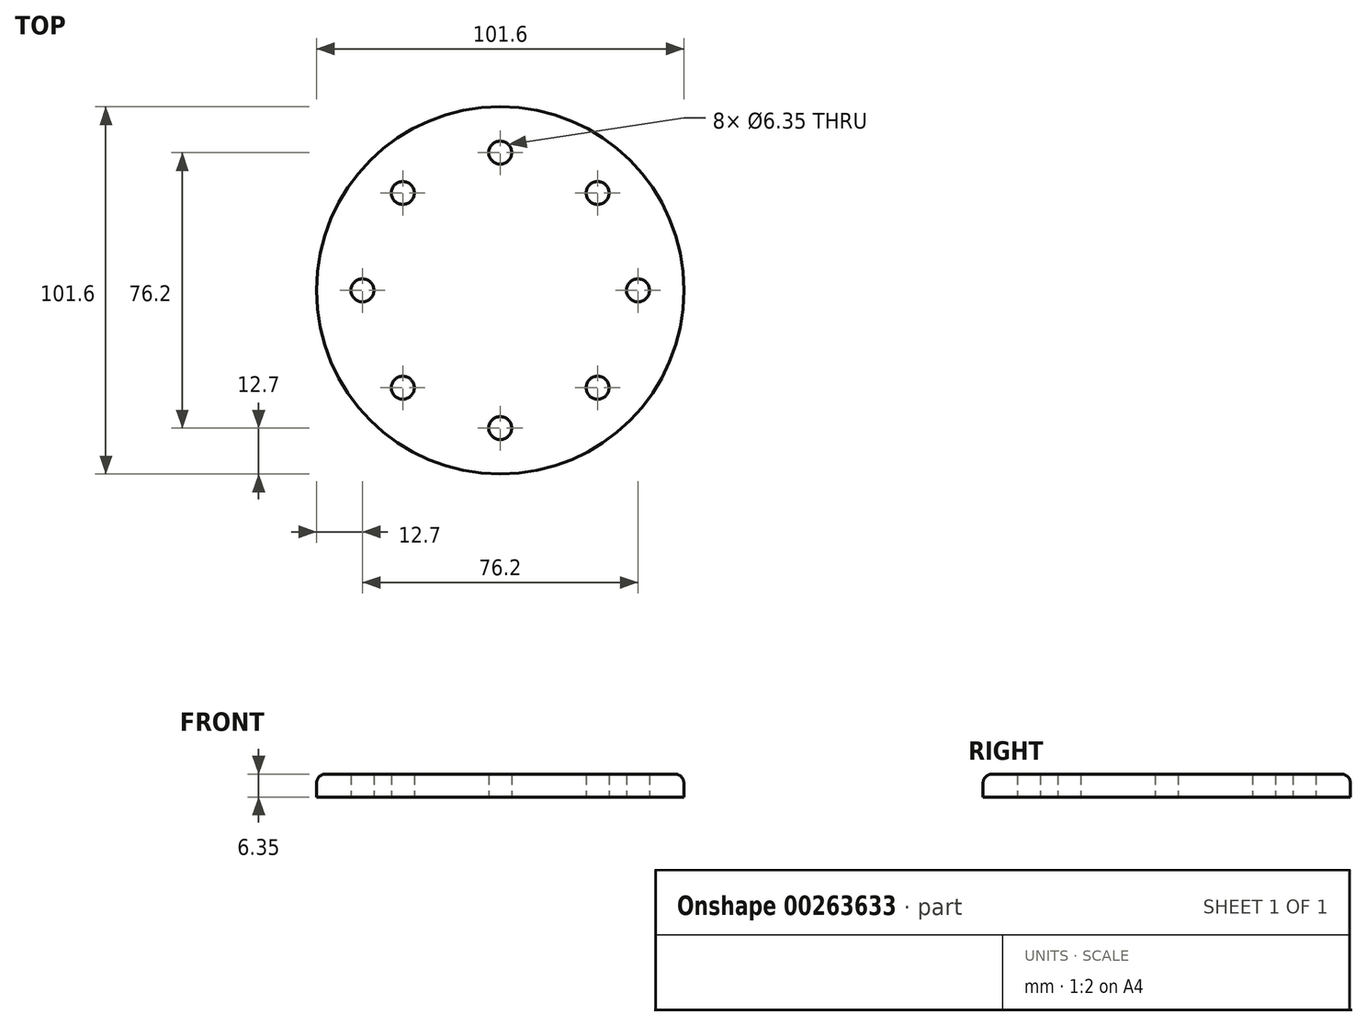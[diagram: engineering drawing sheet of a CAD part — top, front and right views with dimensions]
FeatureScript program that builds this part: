
annotation { "Feature Type Name" : "Feature", "Feature Type Description" : "" }
export const myFeature = defineFeature(function(context is Context, id is Id, definition is map)
    precondition{}
    {
        {
            var Q0;
            Q0=qCreatedBy(makeId("Top.planeOp"),FACE);
            var sketch = newSketch(context, id + "F0", { "sketchPlane" : qUnion([Q0])});
            skCircle(sketch, "E0", {"center": v(0, 0) * mm, "radius": 50.8 * mm});
            skCircle(sketch, "E1", {"center": v(-38.1, 0) * mm, "radius": 3.18 * mm});
            skCircle(sketch, "E2", {"center": v(-26.94, -26.94) * mm, "radius": 3.18 * mm});
            skCircle(sketch, "E3", {"center": v(0, -38.1) * mm, "radius": 3.18 * mm});
            skCircle(sketch, "E4", {"center": v(26.94, -26.94) * mm, "radius": 3.18 * mm});
            skCircle(sketch, "E5", {"center": v(38.1, 0) * mm, "radius": 3.18 * mm});
            skCircle(sketch, "E6", {"center": v(26.94, 26.94) * mm, "radius": 3.18 * mm});
            skCircle(sketch, "E7", {"center": v(0, 38.1) * mm, "radius": 3.18 * mm});
            skCircle(sketch, "E8", {"center": v(-26.94, 26.94) * mm, "radius": 3.18 * mm});
            skSolve(sketch);
        }
        {
            var Q0;
            Q0=makeQuery(id+"F0.imprint","IMPRINT",FACE,{"disambiguationData":[TD([[makeQuery(id+"F0.imprint","IMPRINT",EDGE,{"derivedFrom":sQuery(id+"F0.wireOp",EDGE,"E0")}),1.0]])]});
            extrude(context, id + "F1", {"entities" : qUnion([Q0]), "depth" : 6.35 * mm});
        }
        {
            var Q0;
            Q0=sQuery(id+"F0.wireOp",EDGE,"E8");
            extrude(context, id + "F2", {"bodyType" : ToolBodyType.SURFACE, "surfaceEntities" : qUnion([Q0]), "depth" : 19.05 * mm});
        }
        {
            var Q0;
            Q0=sQuery(id+"F0.wireOp",EDGE,"E7");
            extrude(context, id + "F3", {"bodyType" : ToolBodyType.SURFACE, "surfaceEntities" : qUnion([Q0]), "depth" : 19.05 * mm});
        }
        {
            var Q0;
            Q0=sQuery(id+"F0.wireOp",EDGE,"E6");
            extrude(context, id + "F4", {"bodyType" : ToolBodyType.SURFACE, "surfaceEntities" : qUnion([Q0]), "depth" : 19.05 * mm});
        }
        {
            var Q0;
            Q0=sQuery(id+"F0.wireOp",EDGE,"E1");
            extrude(context, id + "F5", {"bodyType" : ToolBodyType.SURFACE, "surfaceEntities" : qUnion([Q0]), "depth" : 19.05 * mm});
        }
        {
            var Q0;
            Q0=sQuery(id+"F0.wireOp",EDGE,"E2");
            extrude(context, id + "F6", {"bodyType" : ToolBodyType.SURFACE, "surfaceEntities" : qUnion([Q0]), "depth" : 19.05 * mm});
        }
        {
            var Q0;
            Q0=sQuery(id+"F0.wireOp",EDGE,"E3");
            extrude(context, id + "F7", {"bodyType" : ToolBodyType.SURFACE, "surfaceEntities" : qUnion([Q0]), "depth" : 19.05 * mm});
        }
        {
            var Q0;
            Q0=sQuery(id+"F0.wireOp",EDGE,"E4");
            extrude(context, id + "F8", {"bodyType" : ToolBodyType.SURFACE, "surfaceEntities" : qUnion([Q0]), "depth" : 19.05 * mm});
        }
        {
            var Q0;
            Q0=sQuery(id+"F0.wireOp",EDGE,"E5");
            extrude(context, id + "F9", {"bodyType" : ToolBodyType.SURFACE, "surfaceEntities" : qUnion([Q0]), "depth" : 19.05 * mm});
        }
        {
            var Q0;
            Q0=makeQuery(id+"F1.opExtrude","CAP_EDGE",EDGE,{"disambiguationData":[OSD([sQuery(id+"F0.wireOp",EDGE,"E0")])],"isStart":false});
            fillet(context, id + "F10", {"entities" : qUnion([Q0]), "radius" : 2.54 * mm, "tangentPropagation" : true, "allowEdgeOverflow" : false});
        }
    });
